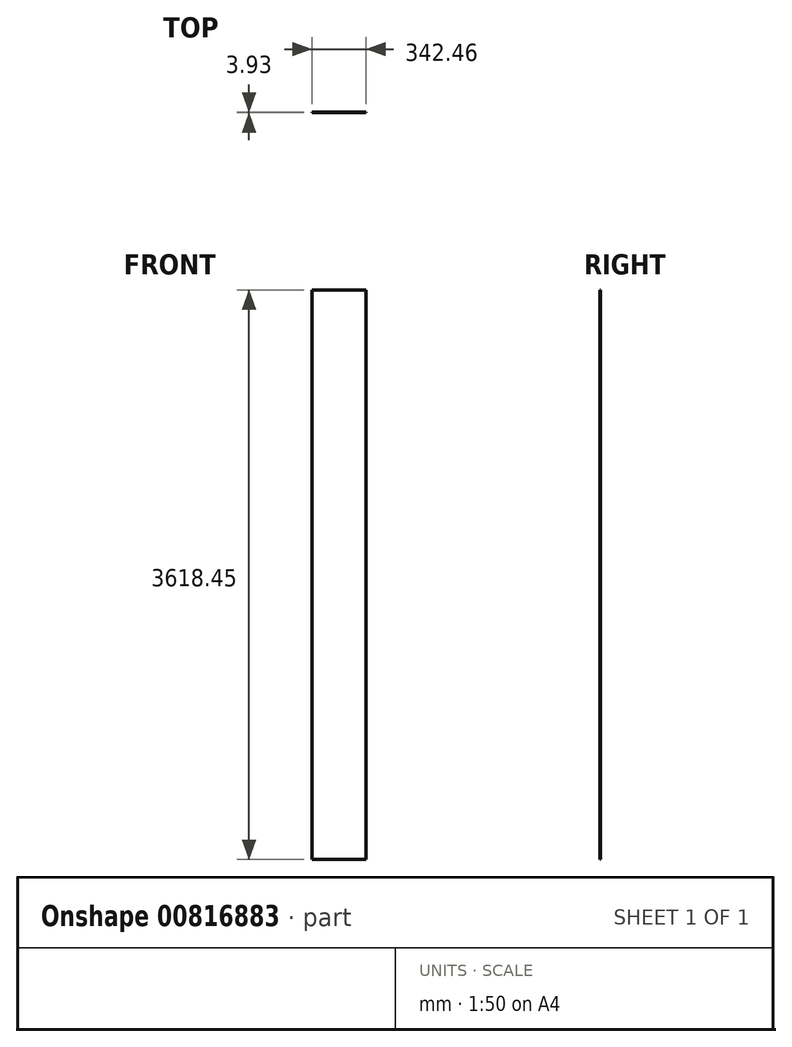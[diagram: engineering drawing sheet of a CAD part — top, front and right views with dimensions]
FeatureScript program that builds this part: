
annotation { "Feature Type Name" : "Feature", "Feature Type Description" : "" }
export const myFeature = defineFeature(function(context is Context, id is Id, definition is map)
    precondition{}
    {
        {
            var Q0;
            Q0=qCreatedBy(makeId("Front.planeOp"),FACE);
            var sketch = newSketch(context, id + "F0", { "sketchPlane" : qUnion([Q0])});
            skLineSegment(sketch, "E0.bottom", {"start": v(-202.5, -5050.27) * mm, "end": v(-544.96, -5050.27) * mm});
            skLineSegment(sketch, "E0.top", {"start": v(-202.5, -8668.72) * mm, "end": v(-544.96, -8668.72) * mm});
            skLineSegment(sketch, "E0.left", {"start": v(-202.5, -5050.27) * mm, "end": v(-202.5, -8668.72) * mm});
            skLineSegment(sketch, "E0.right", {"start": v(-544.96, -5050.27) * mm, "end": v(-544.96, -8668.72) * mm});
            skSolve(sketch);
        }
        {
            var Q0;
            Q0 = qSketchRegion(id + "F0", true);
            extrude(context, id + "F1", {"entities" : qUnion([Q0]), "depth" : 3.93 * mm, "offsetDistance" : 25.4 * mm});
        }
    });
